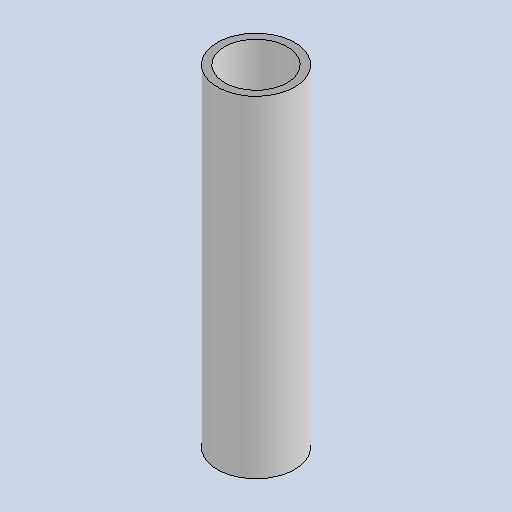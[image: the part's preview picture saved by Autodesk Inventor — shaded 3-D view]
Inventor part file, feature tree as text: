
AUTODESK INVENTOR PART (.ipt)
format: ipt  version: 2025.1 (Build 291241020, 241B)  size: 120,320 bytes
history: native  units: mm
features: extrude x1, sketch x1
ambient origin geometry x8: Origin, YZ Plane, XZ Plane, XY Plane, X Axis, Y Axis, Z Axis, Center Point
bodies: Body1 (feature_tree)
feature tree (2):
  extrude  "Extrusion5"  Depth=90.0mm
  sketch  "Sketch11"  dims[d187=21.0mm d188=2.0mm d189=90.0mm d190=0.0mm]
